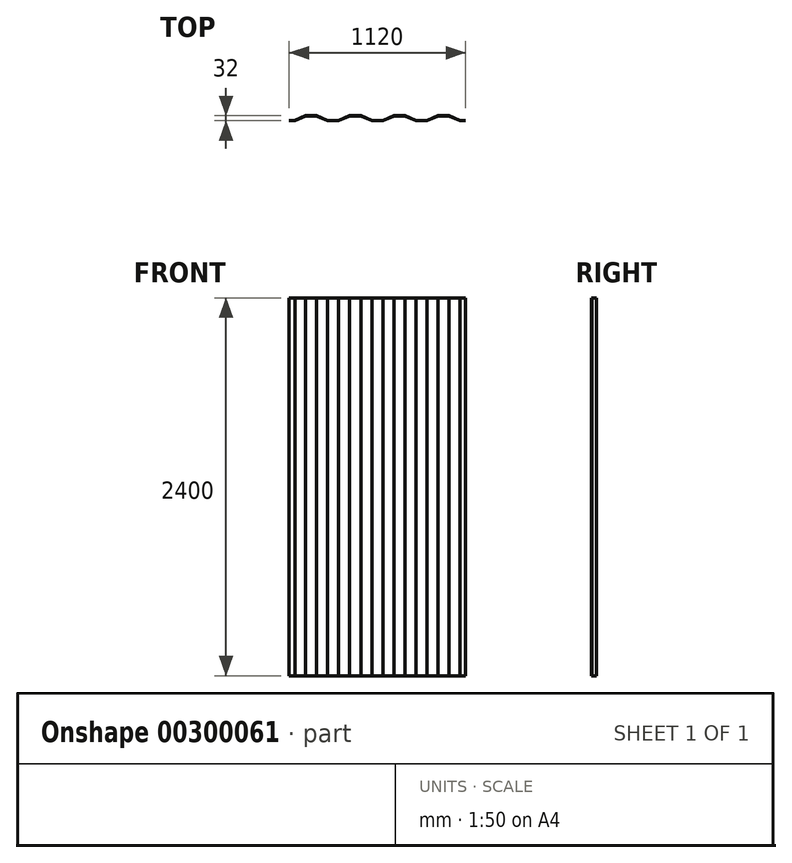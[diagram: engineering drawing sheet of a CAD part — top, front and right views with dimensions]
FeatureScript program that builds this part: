
annotation { "Feature Type Name" : "Feature", "Feature Type Description" : "" }
export const myFeature = defineFeature(function(context is Context, id is Id, definition is map)
    precondition{}
    {
        {
            var Q0;
            Q0=qCreatedBy(makeId("Top.planeOp"),FACE);
            var sketch = newSketch(context, id + "F0", { "sketchPlane" : qUnion([Q0])});
            skLineSegment(sketch, "E0", {"start": v(0, 0) * mm, "end": v(35, 0) * mm});
            skLineSegment(sketch, "E1", {"start": v(105, 30) * mm, "end": v(35, 0) * mm});
            skLineSegment(sketch, "E2", {"start": v(105, 30) * mm, "end": v(175, 30) * mm});
            skLineSegment(sketch, "E3", {"start": v(245, 0) * mm, "end": v(175, 30) * mm});
            skLineSegment(sketch, "E4", {"start": v(245, 0) * mm, "end": v(315, 0) * mm});
            skLineSegment(sketch, "E5", {"start": v(385, 30) * mm, "end": v(315, 0) * mm});
            skLineSegment(sketch, "E6", {"start": v(385, 30) * mm, "end": v(455, 30) * mm});
            skLineSegment(sketch, "E7", {"start": v(525, 0) * mm, "end": v(455, 30) * mm});
            skLineSegment(sketch, "E8", {"start": v(525, 0) * mm, "end": v(595, 0) * mm});
            skLineSegment(sketch, "E9", {"start": v(665, 30) * mm, "end": v(595, 0) * mm});
            skLineSegment(sketch, "E10", {"start": v(665, 30) * mm, "end": v(735, 30) * mm});
            skLineSegment(sketch, "E11", {"start": v(805, 0) * mm, "end": v(735, 30) * mm});
            skLineSegment(sketch, "E12", {"start": v(805, 0) * mm, "end": v(875, 0) * mm});
            skLineSegment(sketch, "E13", {"start": v(945, 30) * mm, "end": v(875, 0) * mm});
            skLineSegment(sketch, "E14", {"start": v(945, 30) * mm, "end": v(1015, 30) * mm});
            skLineSegment(sketch, "E15", {"start": v(1085, 0) * mm, "end": v(1120, 0) * mm});
            skLineSegment(sketch, "E16", {"start": v(0, 0) * mm, "end": v(0, -2) * mm});
            skLineSegment(sketch, "E17", {"start": v(0, -2) * mm, "end": v(37, -2) * mm});
            skLineSegment(sketch, "E18", {"start": v(105, 28) * mm, "end": v(37, -2) * mm});
            skLineSegment(sketch, "E19", {"start": v(105, 28) * mm, "end": v(175, 28) * mm});
            skLineSegment(sketch, "E20", {"start": v(245, -2) * mm, "end": v(315, -2) * mm});
            skLineSegment(sketch, "E21", {"start": v(385, 28) * mm, "end": v(455, 28) * mm});
            skLineSegment(sketch, "E22", {"start": v(525, -2) * mm, "end": v(455, 28) * mm});
            skLineSegment(sketch, "E23", {"start": v(525, -2) * mm, "end": v(595, -2) * mm});
            skLineSegment(sketch, "E24", {"start": v(665, 28) * mm, "end": v(735, 28) * mm});
            skLineSegment(sketch, "E25", {"start": v(385, 28) * mm, "end": v(315, -2) * mm});
            skLineSegment(sketch, "E26", {"start": v(175, 28) * mm, "end": v(245, -2) * mm});
            skLineSegment(sketch, "E27", {"start": v(665, 28) * mm, "end": v(595, -2) * mm});
            skLineSegment(sketch, "E28", {"start": v(805, -2) * mm, "end": v(735, 28) * mm});
            skLineSegment(sketch, "E29", {"start": v(805, -2) * mm, "end": v(875, -2) * mm});
            skLineSegment(sketch, "E30", {"start": v(945, 28) * mm, "end": v(1015, 28) * mm});
            skLineSegment(sketch, "E31", {"start": v(1015, 30) * mm, "end": v(1085, 0) * mm});
            skLineSegment(sketch, "E32", {"start": v(1085, -2) * mm, "end": v(1015, 28) * mm});
            skLineSegment(sketch, "E33", {"start": v(1120, 0) * mm, "end": v(1120, -2) * mm});
            skLineSegment(sketch, "E34", {"start": v(1120, -2) * mm, "end": v(1085, -2) * mm});
            skLineSegment(sketch, "E35", {"start": v(945, 28) * mm, "end": v(875, -2) * mm});
            skSolve(sketch);
        }
        {
            var Q0;
            Q0 = qSketchRegion(id + "F0", true);
            extrude(context, id + "F1", {"entities" : qUnion([Q0]), "depth" : 2400 * mm});
        }
    });
